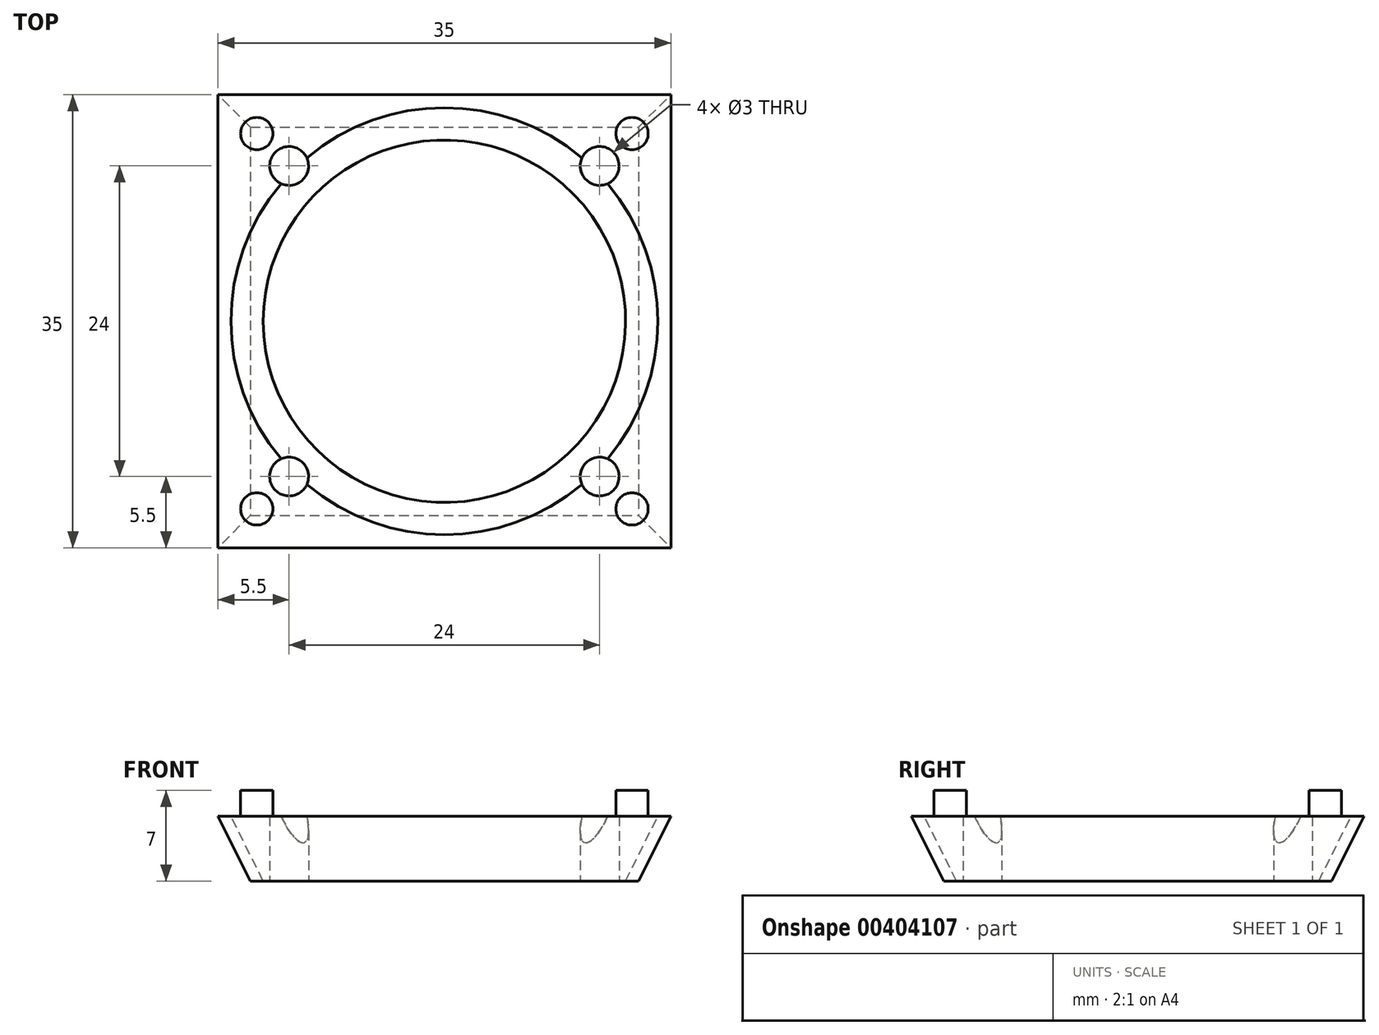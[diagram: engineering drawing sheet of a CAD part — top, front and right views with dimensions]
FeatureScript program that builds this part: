
annotation { "Feature Type Name" : "Feature", "Feature Type Description" : "" }
export const myFeature = defineFeature(function(context is Context, id is Id, definition is map)
    precondition{}
    {
        {
            var Q0;
            Q0=qCreatedBy(makeId("Top.planeOp"),FACE);
            var sketch = newSketch(context, id + "F0", { "sketchPlane" : qUnion([Q0])});
            skLineSegment(sketch, "E0.bottom", {"start": v(0, 0) * mm, "end": v(30, 0) * mm});
            skLineSegment(sketch, "E0.top", {"start": v(0, -30) * mm, "end": v(30, -30) * mm});
            skLineSegment(sketch, "E0.left", {"start": v(0, 0) * mm, "end": v(0, -30) * mm});
            skLineSegment(sketch, "E0.right", {"start": v(30, 0) * mm, "end": v(30, -30) * mm});
            skPoint(sketch, "E1", {"position": v(15, -30) * mm});
            skPoint(sketch, "E2", {"position": v(30, -15) * mm});
            skSolve(sketch);
        }
        {
            var Q0;
            Q0=qCreatedBy(makeId("Top.planeOp"),FACE);
            cPlane(context, id + "F1", {"entities" : qUnion([Q0]), "cplaneType" : CPlaneType.OFFSET, "offset" : 5 * mm, "width" : 150 * mm, "height" : 150 * mm});
        }
        {
            var Q0;
            Q0=qCreatedBy(id+"F1.planeOp",FACE);
            var sketch = newSketch(context, id + "F2", { "sketchPlane" : qUnion([Q0])});
            skLineSegment(sketch, "E3.bottom", {"start": v(-2.5, 2.5) * mm, "end": v(32.5, 2.5) * mm});
            skLineSegment(sketch, "E3.top", {"start": v(-2.5, -32.5) * mm, "end": v(32.5, -32.5) * mm});
            skLineSegment(sketch, "E3.left", {"start": v(-2.5, 2.5) * mm, "end": v(-2.5, -32.5) * mm});
            skLineSegment(sketch, "E3.right", {"start": v(32.5, 2.5) * mm, "end": v(32.5, -32.5) * mm});
            skPoint(sketch, "E4", {"position": v(15, -32.5) * mm});
            skPoint(sketch, "E5", {"position": v(32.5, -15) * mm});
            skSolve(sketch);
        }
        {
            var Q0;
            Q0=qSketchRegion(id+"F0",true);
            var Q1;
            Q1=qSketchRegion(id+"F2",true);
            loft(context, id + "F3", {"sheetProfilesArray" : [{ "sheetProfileEntities" : qUnion([Q0]) }, { "sheetProfileEntities" : qUnion([Q1]) }]});
        }
        {
            var Q0;
            Q0=makeQuery(id+"F3.opLoft","CAP_FACE",FACE,{"disambiguationData":[OSD([makeQuery(id+"F2.imprint","IMPRINT",FACE,{"disambiguationData":[TD([[makeQuery(id+"F2.imprint","IMPRINT",EDGE,{"derivedFrom":sQuery(id+"F2.wireOp",EDGE,"E3.bottom")}),-1.0]])]})])],"isStart":true});
            var sketch = newSketch(context, id + "F4", { "sketchPlane" : qUnion([Q0])});
            skCircle(sketch, "E6", {"center": v(15, -15) * mm, "radius": 16.5 * mm});
            skSolve(sketch);
        }
        {
            var Q0;
            Q0=makeQuery(id+"F3.opLoft","CAP_FACE",FACE,{"disambiguationData":[OSD([makeQuery(id+"F0.imprint","IMPRINT",FACE,{"disambiguationData":[TD([[makeQuery(id+"F0.imprint","IMPRINT",EDGE,{"derivedFrom":sQuery(id+"F0.wireOp",EDGE,"E0.bottom")}),-1.0]])]})])],"isStart":true});
            var sketch = newSketch(context, id + "F5", { "sketchPlane" : qUnion([Q0])});
            skCircle(sketch, "E7", {"center": v(15, 15) * mm, "radius": 14 * mm});
            skSolve(sketch);
        }
        {
            var Q1;
            Q1=qSketchRegion(id+"F4",true);
            var Q2;
            Q2=qSketchRegion(id+"F5",true);
            loft(context, id + "F6", {"operationType" : NewBodyOperationType.REMOVE, "sheetProfilesArray" : [{ "sheetProfileEntities" : qUnion([Q1]) }, { "sheetProfileEntities" : qUnion([Q2]) }]});
        }
        {
            var Q0;
            Q0=makeQuery(id+"F2.imprint","IMPRINT",FACE,{"disambiguationData":[TD([[makeQuery(id+"F2.imprint","IMPRINT",EDGE,{"derivedFrom":sQuery(id+"F2.wireOp",EDGE,"E3.bottom")}),-1.0]])]});
            var sketch = newSketch(context, id + "F7", { "sketchPlane" : qUnion([Q0])});
            skCircle(sketch, "E8", {"center": v(0.5, -0.5) * mm, "radius": 1.25 * mm});
            skCircle(sketch, "E9", {"center": v(29.5, -0.5) * mm, "radius": 1.25 * mm});
            skCircle(sketch, "E10", {"center": v(29.5, -29.5) * mm, "radius": 1.25 * mm});
            skCircle(sketch, "E11", {"center": v(0.5, -29.5) * mm, "radius": 1.25 * mm});
            skSolve(sketch);
        }
        {
            var Q0;
            Q0=qSketchRegion(id+"F7",true);
            extrude(context, id + "F8", {"entities" : qUnion([Q0]), "operationType" : NewBodyOperationType.ADD, "depth" : 2 * mm});
        }
        {
            var Q0;
            Q0=makeQuery(id+"F0.imprint","IMPRINT",FACE,{"disambiguationData":[TD([[makeQuery(id+"F0.imprint","IMPRINT",EDGE,{"derivedFrom":sQuery(id+"F0.wireOp",EDGE,"E0.bottom")}),-1.0]])]});
            var sketch = newSketch(context, id + "F9", { "sketchPlane" : qUnion([Q0])});
            skCircle(sketch, "E12", {"center": v(27, -27) * mm, "radius": 1.5 * mm});
            skCircle(sketch, "E13", {"center": v(3, -27) * mm, "radius": 1.5 * mm});
            skCircle(sketch, "E14", {"center": v(3, -3) * mm, "radius": 1.5 * mm});
            skCircle(sketch, "E15", {"center": v(27, -3) * mm, "radius": 1.5 * mm});
            skSolve(sketch);
        }
        {
            var Q0;
            Q0=qSketchRegion(id+"F9",true);
            extrude(context, id + "F10", {"entities" : qUnion([Q0]), "operationType" : NewBodyOperationType.REMOVE, "depth" : 5 * mm});
        }
    });
